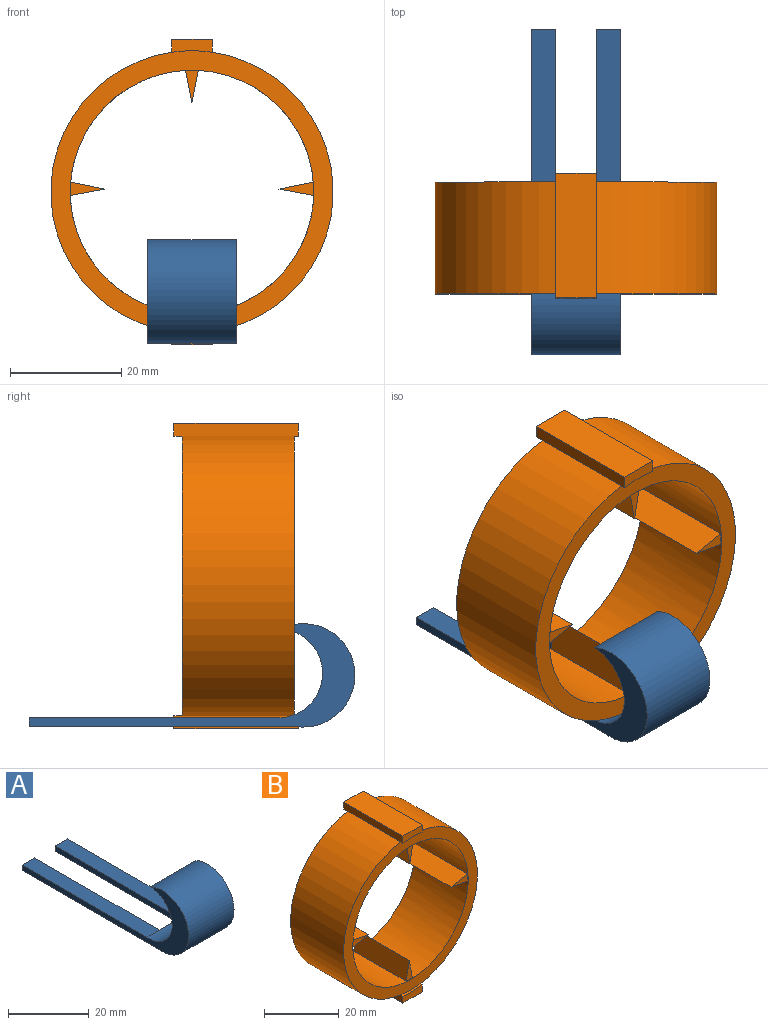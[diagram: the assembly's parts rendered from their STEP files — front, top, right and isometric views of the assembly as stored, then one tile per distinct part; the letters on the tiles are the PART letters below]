
ASSEMBLY  parts=2 mates=1
PART A: 12 faces, bbox 15.9x58.5x18.6 mm
  f0: plane 4.34x1.61mm, normal (0,1,0), area 7mm2, adj f1,f2,f7,f9
  f1: plane 43.84x4.34mm, normal (0,0,1), area 190.5mm2, adj f0,f5,f7,f9
  f2: plane 47.92x15.93mm, normal (0,0,-1), area 445.9mm2, adj f0,f3,f6,f7,f8,f9,f10,f11
  f3: plane 4.34x1.61mm, normal (0,1,0), area 7mm2, adj f2,f4,f8,f10
  f4: plane 43.84x4.34mm, normal (0,0,1), area 190.5mm2, adj f3,f5,f8,f10
  f5: cylinder r=7.99mm len=15.97mm, axis (-1,0,0), area 405.9mm2, adj f1,f4,f6,f7,f8,f11
  f6: cylinder r=9.28mm len=18.56mm, axis (-1,0,0), area 551.5mm2, adj f2,f5,f7,f8
  f7: plane 58.47x18.56mm, normal (1,0,0), area 188.6mm2, adj f0,f1,f2,f5,f6
  f8: plane 58.47x18.56mm, normal (-1,0,0), area 188.6mm2, adj f2,f3,f4,f5,f6
  f9: plane 43.84x1.61mm, normal (-1,0,0), area 70.5mm2, adj f0,f1,f2,f11
  f10: plane 43.84x1.61mm, normal (1,0,0), area 70.5mm2, adj f2,f3,f4,f11
  f11: plane 7.24x1.61mm, normal (0,1,0), area 11.6mm2, adj f2,f5,f9,f10
PART B: 31 faces, bbox 50.7x22.4x54.7 mm
  f0: cylinder r=21.85mm len=43.71mm, axis (0,1,0), area 2567.4mm2, adj f3,f4,f19,f20,f21,f22,f23,f24
  f1: cylinder r=25.33mm len=50.15mm, axis (0,1,0), area 1451.4mm2, adj f3,f4,f7,f13
  f2: cylinder r=25.33mm len=50.15mm, axis (0,1,0), area 1451.4mm2, adj f3,f4,f9,f15
  f3: plane 50.67x50.67mm, normal (0,-1,0), area 516mm2, adj f0,f1,f2,f5,f12
  f4: plane 50.67x50.67mm, normal (0,1,0), area 545.1mm2, adj f0,f1,f2,f6,f14,f20,f21,f23
  f5: cylinder r=25.33mm len=7.24mm, axis (0,1,0), area 5.5mm2, adj f3,f7,f9,f10
  f6: cylinder r=25.33mm len=7.24mm, axis (0,1,0), area 11.1mm2, adj f4,f7,f9,f11
  f7: plane 22.35x2.29mm, normal (1,0,0), area 51.2mm2, adj f1,f5,f6,f8,f10,f11
  f8: plane 22.35x7.24mm, normal (0,0,-1), area 161.7mm2, adj f7,f9,f10,f11
  f9: plane 22.35x2.29mm, normal (-1,0,0), area 51.2mm2, adj f2,f5,f6,f8,f10,f11
  f10: plane 7.24x2.29mm, normal (0,-1,0), area 15.3mm2, adj f5,f7,f8,f9
  f11: plane 7.24x2.29mm, normal (0,1,0), area 15.3mm2, adj f6,f7,f8,f9
  f12: cylinder r=25.33mm len=7.24mm, axis (0,1,0), area 5.5mm2, adj f3,f13,f15,f17
  f13: plane 22.35x2.29mm, normal (1,0,0), area 51.2mm2, adj f1,f12,f14,f16,f17,f18
  f14: cylinder r=25.33mm len=7.24mm, axis (0,1,0), area 11.1mm2, adj f4,f13,f15,f18
  f15: plane 22.35x2.29mm, normal (-1,0,0), area 51.2mm2, adj f2,f12,f14,f16,f17,f18
  f16: plane 22.35x7.24mm, normal (0,0,1), area 161.7mm2, adj f13,f15,f17,f18
  f17: plane 7.24x2.29mm, normal (0,-1,0), area 15.3mm2, adj f12,f13,f15,f16
  f18: plane 7.24x2.29mm, normal (0,1,0), area 15.3mm2, adj f13,f14,f15,f16
  f19: plane 5.87x2.28mm, normal (0,-1,0), area 6.7mm2, adj f0,f20,f21
  f20: plane 19.81x5.84mm, normal (-0.98,0,-0.19), area 117.8mm2, adj f0,f4,f19,f21
  f21: plane 19.81x5.84mm, normal (0.98,0,-0.19), area 117.9mm2, adj f0,f4,f19,f20
  f22: plane 6.14x2.38mm, normal (0,-1,0), area 7.3mm2, adj f0,f23,f24
  f23: plane 19.81x6.09mm, normal (-0.98,0,0.2), area 123.2mm2, adj f0,f4,f22,f24
  f24: plane 19.81x6.12mm, normal (0.98,0,0.18), area 123.2mm2, adj f0,f4,f22,f23
  f25: plane 6.22x2.41mm, normal (0,-1,0), area 7.5mm2, adj f0,f26,f27
  f26: plane 19.81x6.14mm, normal (0.2,0,0.98), area 124.2mm2, adj f0,f4,f25,f27
  f27: plane 19.81x6.21mm, normal (0.18,0,-0.98), area 125mm2, adj f0,f4,f25,f26
  f28: plane 6.24x2.42mm, normal (0,-1,0), area 7.6mm2, adj f0,f29,f30
  f29: plane 19.81x6.24mm, normal (-0.18,0,-0.98), area 125.6mm2, adj f0,f4,f28,f30
  f30: plane 19.81x6.17mm, normal (-0.2,0,0.98), area 124.8mm2, adj f0,f4,f28,f29
PLACE A t=(-30.09,18.29,-29.17)mm
PLACE B t=(-106.81,8.84,-2.14)mm
MATE planar B.f9 <-> A.f10  axis (-1,0,0) through (-25.74,-0.81,-28.36)mm
